# Revit family: 热交换器 - 汽-水 - 屉式2020
name_source: partatom
category: 机械设备
units: mm (PartAtom-declared; Revit-internal decimal feet)

## family parameters
共享 = 否
加载时剪切的空心 = 否
圆形连接件大小 = 使用半径
基于工作平面 = 否
总是垂直 = 是
房间计算点 = 否
零件类型 = 标准

## types (3) — shared parameters
URL = www.goujianwu.com
供水温度 = 60 °C
冷凝法兰厚度 = 20.00 mm
回水温度 = 50 °C
基座宽度 = 2000.00 mm
基座长度 = 2000.00 mm
基座高度 = 2000.00 mm
安全阀半径 = 25.00 mm
安全阀法兰半径 = 82.50 mm
安全阀法兰厚度 = 20.00 mm
安全阀法兰直径 = 165.00 mm
安全阀直径 = 50.00 mm
排气阀半径 = 7.50 mm
排气阀法兰半径 = 47.50 mm
排气阀法兰厚度 = 14.00 mm
排气阀法兰直径 = 95.00 mm
排气阀直径 = 15.00 mm
热交换器材质 = <按类别>
蒸汽法兰厚度 = 22.00 mm
说明 = 永久免费族库下载，找构件就上构件坞
默认高程 = 0.00 mm

## per-type parameters (varying)
- DN400: 供水半径=75.00 mm; 供水法兰半径=142.50 mm; 供水法兰厚度=24.00 mm; 供水法兰直径=285.00 mm; 供水直径=150.00 mm; 冷凝水管半径=25.00 mm; 冷凝水管直径=50.00 mm; 冷凝法兰半径=82.50 mm; 冷凝法兰直径=165.00 mm; 回水半径=75.00 mm; 回水法兰半径=142.50 mm; 回水法兰厚度=24.00 mm; 回水法兰直径=285.00 mm; 回水直径=150.00 mm; 换热量=1276000 kW; 热交换器半径=200.00 mm; 热交换器直径=400.00 mm; 热交换器长度=2020.00 mm; 热交换器高度=1226.00 mm; 蒸汽半径=50.00 mm; 蒸汽法兰半径=110.00 mm; 蒸汽法兰直径=220.00 mm; 蒸汽直径=100.00 mm; 长度 1=260.00 mm; 长度 2=402.00 mm; 长度 3=210.00 mm; 长度 4=870.00 mm; 长度 5=280.00 mm; 长度 6=120.00 mm; 长度 7=240.00 mm; 高度 1=876.00 mm; 高度 2=350.00 mm
- DN500: 供水半径=75.00 mm; 供水法兰半径=142.50 mm; 供水法兰厚度=24.00 mm; 供水法兰直径=285.00 mm; 供水直径=150.00 mm; 冷凝水管半径=32.50 mm; 冷凝水管直径=65.00 mm; 冷凝法兰半径=92.50 mm; 冷凝法兰直径=185.00 mm; 回水半径=75.00 mm; 回水法兰半径=142.50 mm; 回水法兰厚度=24.00 mm; 回水法兰直径=285.00 mm; 回水直径=150.00 mm; 换热量=1860000 kW; 热交换器半径=250.00 mm; 热交换器直径=500.00 mm; 热交换器长度=2016.00 mm; 热交换器高度=1176.00 mm; 蒸汽半径=62.50 mm; 蒸汽法兰半径=125.00 mm; 蒸汽法兰直径=250.00 mm; 蒸汽直径=125.00 mm; 长度 1=306.00 mm; 长度 2=438.00 mm; 长度 3=300.00 mm; 长度 4=645.00 mm; 长度 5=330.00 mm; 长度 6=150.00 mm; 长度 7=300.00 mm; 高度 1=763.00 mm; 高度 2=413.00 mm
- DN600: 供水半径=125.00 mm; 供水法兰半径=202.50 mm; 供水法兰厚度=26.00 mm; 供水法兰直径=405.00 mm; 供水直径=250.00 mm; 冷凝水管半径=32.50 mm; 冷凝水管直径=65.00 mm; 冷凝法兰半径=92.50 mm; 冷凝法兰直径=185.00 mm; 回水半径=125.00 mm; 回水法兰半径=202.50 mm; 回水法兰厚度=26.00 mm; 回水法兰直径=405.00 mm; 回水直径=250.00 mm; 换热量=3256000 kW; 热交换器半径=300.00 mm; 热交换器直径=600.00 mm; 热交换器长度=2237.00 mm; 热交换器高度=1470.00 mm; 蒸汽半径=62.50 mm; 蒸汽法兰半径=125.00 mm; 蒸汽法兰直径=250.00 mm; 蒸汽直径=125.00 mm; 长度 1=344.00 mm; 长度 2=509.00 mm; 长度 3=290.00 mm; 长度 4=840.00 mm; 长度 5=400.00 mm; 长度 6=180.00 mm; 长度 7=360.00 mm; 高度 1=960.00 mm; 高度 2=510.00 mm
